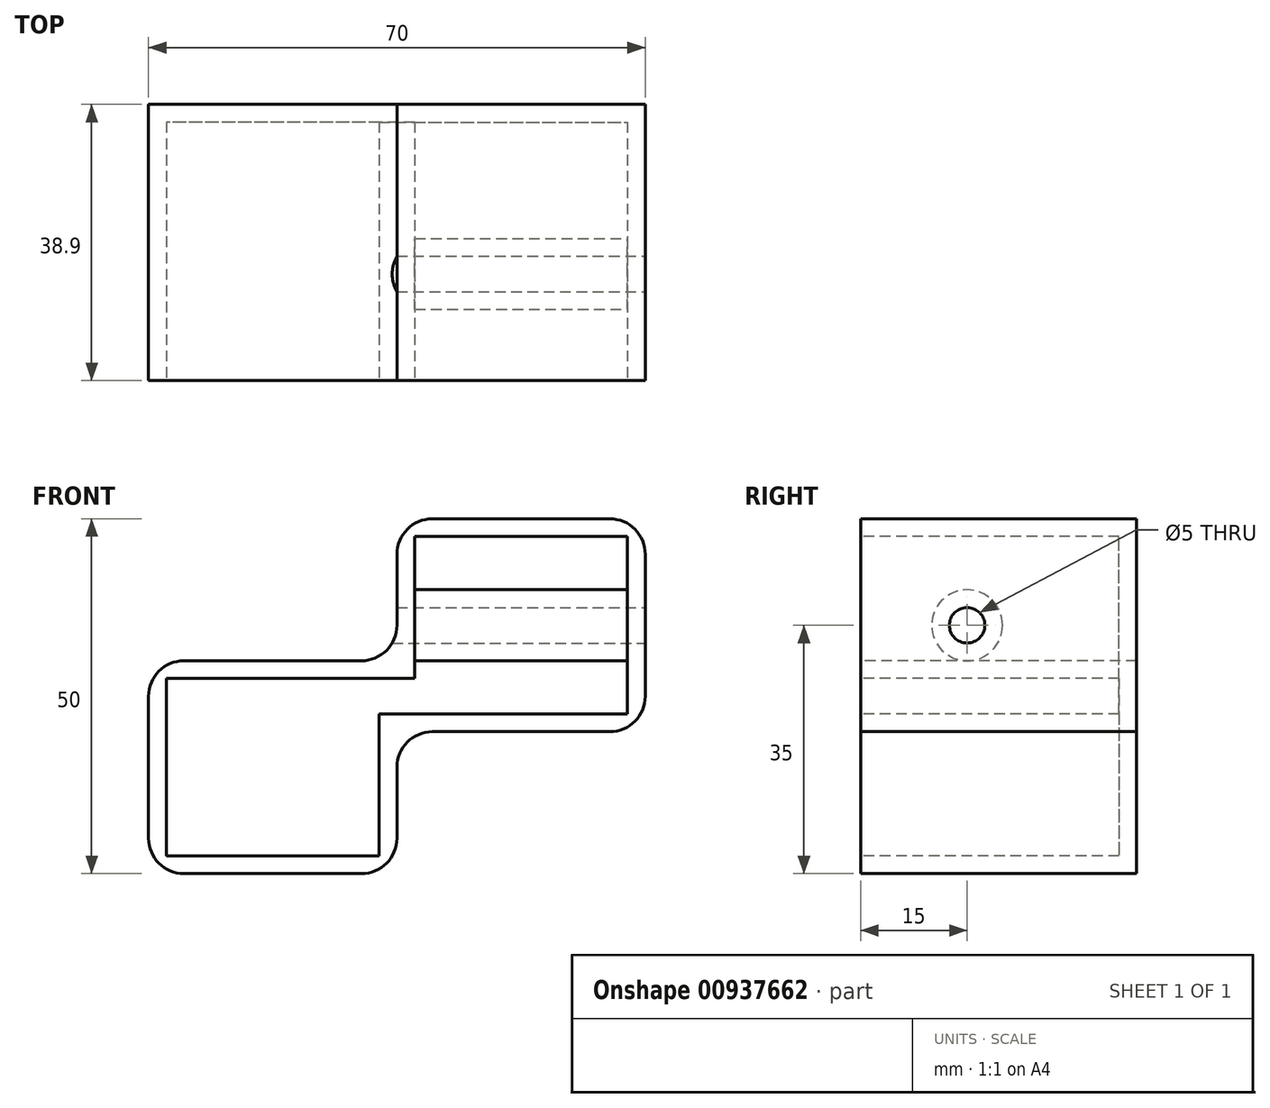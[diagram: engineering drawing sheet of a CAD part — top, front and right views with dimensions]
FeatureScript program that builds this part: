
annotation { "Feature Type Name" : "Feature", "Feature Type Description" : "" }
export const myFeature = defineFeature(function(context is Context, id is Id, definition is map)
    precondition{}
    {
        {
            var Q0;
            Q0=qCreatedBy(makeId("Front.planeOp"),FACE);
            var sketch = newSketch(context, id + "F0", { "sketchPlane" : qUnion([Q0])});
            skLineSegment(sketch, "E0.bottom", {"start": v(0, 0) * mm, "end": v(35, 0) * mm});
            skLineSegment(sketch, "E0.top", {"start": v(0, 30) * mm, "end": v(35, 30) * mm});
            skLineSegment(sketch, "E0.left", {"start": v(0, 0) * mm, "end": v(0, 30) * mm});
            skLineSegment(sketch, "E0.right", {"start": v(35, 0) * mm, "end": v(35, 30) * mm});
            skLineSegment(sketch, "E1.bottom", {"start": v(0, 10) * mm, "end": v(-35, 10) * mm});
            skLineSegment(sketch, "E1.top", {"start": v(0, -20) * mm, "end": v(-35, -20) * mm});
            skLineSegment(sketch, "E1.left", {"start": v(0, 10) * mm, "end": v(0, -20) * mm});
            skLineSegment(sketch, "E1.right", {"start": v(-35, 10) * mm, "end": v(-35, -20) * mm});
            skSolve(sketch);
        }
        {
            var Q0;
            {var subQ1=sQuery(id+"F0.wireOp",EDGE,"E0.bottom");Q0=makeQuery(id+"F0.imprint","IMPRINT",FACE,{"disambiguationData":[TD([[makeQuery(id+"F0.imprint","IMPRINT",EDGE,{"derivedFrom":subQ1}),1.0]])]});}
            var Q1;
            {var subQ3=sQuery(id+"F0.wireOp",EDGE,"E1.bottom");Q1=makeQuery(id+"F0.imprint","IMPRINT",FACE,{"disambiguationData":[TD([[makeQuery(id+"F0.imprint","IMPRINT",EDGE,{"derivedFrom":subQ3}),1.0]])]});}
            extrude(context, id + "F1", {"entities" : qUnion([Q0, Q1]), "oppositeDirection" : true, "depth" : 38.9 * mm, "offsetDistance" : 25 * mm});
        }
        {
            var Q0;
            Q0=makeQuery(id+"F1.opExtrude","SWEPT_FACE",FACE,{"disambiguationData":[OSD([sQuery(id+"F0.wireOp",EDGE,"E0.right")])]});
            var sketch = newSketch(context, id + "F2", { "sketchPlane" : qUnion([Q0])});
            skCircle(sketch, "E2", {"center": v(15, 15) * mm, "radius": 7.5 * mm});
            skSolve(sketch);
        }
        {
            var Q0;
            Q0=sQuery(id+"F2.wireOp",VERTEX,"E2.center");
            var Q1;
            Q1=makeQuery(id+"F1.opExtrude","SWEPT_BODY",BODY,{"disambiguationData":[OSD([sQuery(id+"F0.wireOp",EDGE,"E0.bottom"),sQuery(id+"F0.wireOp",EDGE,"E0.top"),sQuery(id+"F0.wireOp",EDGE,"E0.left"),sQuery(id+"F0.wireOp",EDGE,"E0.right"),sQuery(id+"F0.wireOp",EDGE,"E1.bottom"),sQuery(id+"F0.wireOp",EDGE,"E1.top"),sQuery(id+"F0.wireOp",EDGE,"E1.left"),sQuery(id+"F0.wireOp",EDGE,"E1.right")])]});
            hole(context, id + "F3", {"style" : HoleStyle.SIMPLE, "endStyle" : HoleEndStyle.THROUGH, "standardTappedOrClearance" : lookupTablePath({ "standard" : "ISO", "size" : "5", "type" : "Drilled" }), "standardBlindInLast" : lookupTablePath({ "standard" : "ISO", "size" : "5", "type" : "Drilled" }), "holeDiameter" : 5 * mm, "majorDiameter" : 4 * mm, "isTappedThrough" : true, "tappedDepth" : 12 * mm, "tapClearance" : 3, "locations" : qUnion([Q0]), "scope" : qUnion([Q1])});
        }
        {
            var Q0;
            Q0=makeQuery(id+"F1.opExtrude","CAP_FACE",FACE,{"disambiguationData":[OSD([sQuery(id+"F0.wireOp",EDGE,"E0.bottom"),sQuery(id+"F0.wireOp",EDGE,"E0.top"),sQuery(id+"F0.wireOp",EDGE,"E0.left"),sQuery(id+"F0.wireOp",EDGE,"E0.right"),sQuery(id+"F0.wireOp",EDGE,"E1.bottom"),sQuery(id+"F0.wireOp",EDGE,"E1.top"),sQuery(id+"F0.wireOp",EDGE,"E1.left"),sQuery(id+"F0.wireOp",EDGE,"E1.right")])],"isStart":true});
            shell(context, id + "F4", {"entities" : qUnion([Q0]), "thickness" : 2.5 * mm});
        }
        {
            var Q0;
            Q0=makeQuery(id+"F1.opExtrude","SWEPT_EDGE",EDGE,{"disambiguationData":[OSD([sQuery(id+"F0.wireOp",EDGE,"E1.bottom"),sQuery(id+"F0.wireOp",EDGE,"E1.right")])]});
            var Q1;
            Q1=makeQuery(id+"F1.opExtrude","SWEPT_EDGE",EDGE,{"disambiguationData":[OSD([sQuery(id+"F0.wireOp",EDGE,"E1.top"),sQuery(id+"F0.wireOp",EDGE,"E1.left")])]});
            var Q2;
            Q2=makeQuery(id+"F1.opExtrude","SWEPT_EDGE",EDGE,{"disambiguationData":[OSD([sQuery(id+"F0.wireOp",EDGE,"E0.bottom"),sQuery(id+"F0.wireOp",EDGE,"E0.right")])]});
            var Q3;
            Q3=makeQuery(id+"F1.opExtrude","SWEPT_EDGE",EDGE,{"disambiguationData":[OSD([sQuery(id+"F0.wireOp",EDGE,"E0.top"),sQuery(id+"F0.wireOp",EDGE,"E0.left")])]});
            var Q4;
            Q4=makeQuery(id+"F1.opExtrude","SWEPT_EDGE",EDGE,{"disambiguationData":[OSD([sQuery(id+"F0.wireOp",EDGE,"E1.top"),sQuery(id+"F0.wireOp",EDGE,"E1.right")])]});
            var Q5;
            Q5=makeQuery(id+"F1.opExtrude","SWEPT_EDGE",EDGE,{"disambiguationData":[OSD([sQuery(id+"F0.wireOp",EDGE,"E0.top"),sQuery(id+"F0.wireOp",EDGE,"E0.right")])]});
            var Q6;
            Q6=makeQuery(id+"F1.opExtrude","SWEPT_EDGE",EDGE,{"disambiguationData":[OSD([sQuery(id+"F0.wireOp",EDGE,"E0.left"),sQuery(id+"F0.wireOp",EDGE,"E1.bottom"),sQuery(id+"F0.wireOp",EDGE,"E1.left")])]});
            var Q7;
            Q7=makeQuery(id+"F1.opExtrude","SWEPT_EDGE",EDGE,{"disambiguationData":[OSD([sQuery(id+"F0.wireOp",EDGE,"E0.bottom"),sQuery(id+"F0.wireOp",EDGE,"E1.left")])]});
            fillet(context, id + "F5", {"entities" : qUnion([Q0, Q1, Q2, Q3, Q4, Q5, Q6, Q7]), "radius" : 5 * mm, "tangentPropagation" : true, "allowEdgeOverflow" : false});
        }
    });
